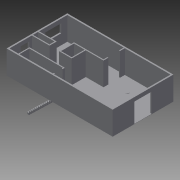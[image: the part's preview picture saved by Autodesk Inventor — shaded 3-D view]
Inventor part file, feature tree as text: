
AUTODESK INVENTOR PART (.ipt)
format: ipt  version: 2014 (Build 180170000, 170)  size: 461,824 bytes
history: native  units: in
note: dims shown in document units (in); Inventor stores cm internally (conversion verified against a paired STEP export)
features: extrude x9, projected_geometry x6, sketch x5
ambient origin geometry x8: Origin, YZ Plane, XZ Plane, XY Plane, X Axis, Y Axis, Z Axis, Center Point
bodies: Body1 (feature_tree)
feature tree (20):
  extrude  "Extrusion7"  Depth=5.0in
  extrude  "Extrusion8"  Depth=72.0in
  extrude  "Extrusion11"  Depth=54.0in
  extrude  "Extrusion12"  Depth=41.0in
  extrude  "Extrusion14"  Depth=93.0in
  extrude  "Extrusion15"  Depth=4.5in
  extrude  "Extrusion17"  Depth=4.5in
  extrude  "Extrusion32"  Depth=4.5in
  extrude  "Instrumentation"  Depth=73.0in
  projected_geometry  "Projected Loop3"
  projected_geometry  "Projected Loop4"
  sketch  "Sketch6"  dims[d1=240.0in d4=5.0in d5=6.0in]
  projected_geometry  "Projected Loop5"
  projected_geometry  "Projected Loop6"
  sketch  "Sketch7"  dims[d14=72.0in d30=72.0in d40=432.0in]
  projected_geometry  "Projected Loop7"
  sketch  "Sketch12"  dims[d57=4.5in d58=60.0in d61=54.0in d64=432.0in]
  sketch  "Sketch23"  dims[d88=6.0in d89=41.0in d90=248.0in]
  projected_geometry  "Projected Loop16"
  sketch  "Sketch24"  dims[d91=37.0in d92=93.0in d93=117.0in d94=4.5in d95=4.5in d96=4.5in d97=73.0in d98=46.0in d99=36.0in d100=6.0in d102=37.0in d103=73.0in d104=39.0in d105=4.5in d106=4.5in d107=4.5in d108=4.5in d109=4.5in d110=263.0in d112=48.0in d117=45.5in d119=240.0in d120=6.0in d122=117.0in d123=90.0in d124=234.0in d125=4.5in d127=4.5in d128=252.0in d129=6.0in d130=46.0in d131=41.0in d132=4.5in d133=73.0in d134=93.0in d135=428.0in d136=97.0in d137=0.0in d138=1.0in d139=0.0in d151=16.0in d152=0.0in d153=66.0in d155=36.0in d156=43.0in d157=25.5in d158=16.0in d159=0.0in d192=35.0in d193=6.0in d195=35.0in d196=0.0in d197=7.25in d198=7.5in d199=7.25in d200=7.5in d201=7.25in d202=7.5in d203=7.25in d204=7.5in d205=7.25in d206=7.5in d207=7.25in d208=7.5in d209=7.25in d210=7.5in d211=7.25in d212=7.5in d213=7.25in d214=7.5in d215=7.25in d216=7.5in d217=7.25in d218=7.5in d219=7.25in d220=7.5in d221=7.25in d222=7.25in d223=7.5in d224=7.5in d225=7.5in d226=7.25in d227=35.0in d228=0.0in d236=84.0in d237=20.25in d238=4.5in d240=0.001in d241=0.0in d370=12.0in d371=12.0in d372=12.0in d373=12.0in d374=12.0in d375=12.0in d377=98.0315in d378=111.811in d379=18.0in d382=64.1732in d383=64.1732in d384=314.1732in d385=314.1732in d386=185.8268in d387=17.5in d388=235.8268in d389=392.126in d390=17.5in d391=12.0in d392=12.0in d393=12.0in d394=12.0in d395=12.0in d396=12.0in d397=12.0in d399=12.0in d400=12.0in d402=12.0in d403=12.0in d404=1.0in d405=0.0in d406=4.5in d407=32.0in d408=1.0in d409=0.0in d411=24.0in d412=90.0deg]
